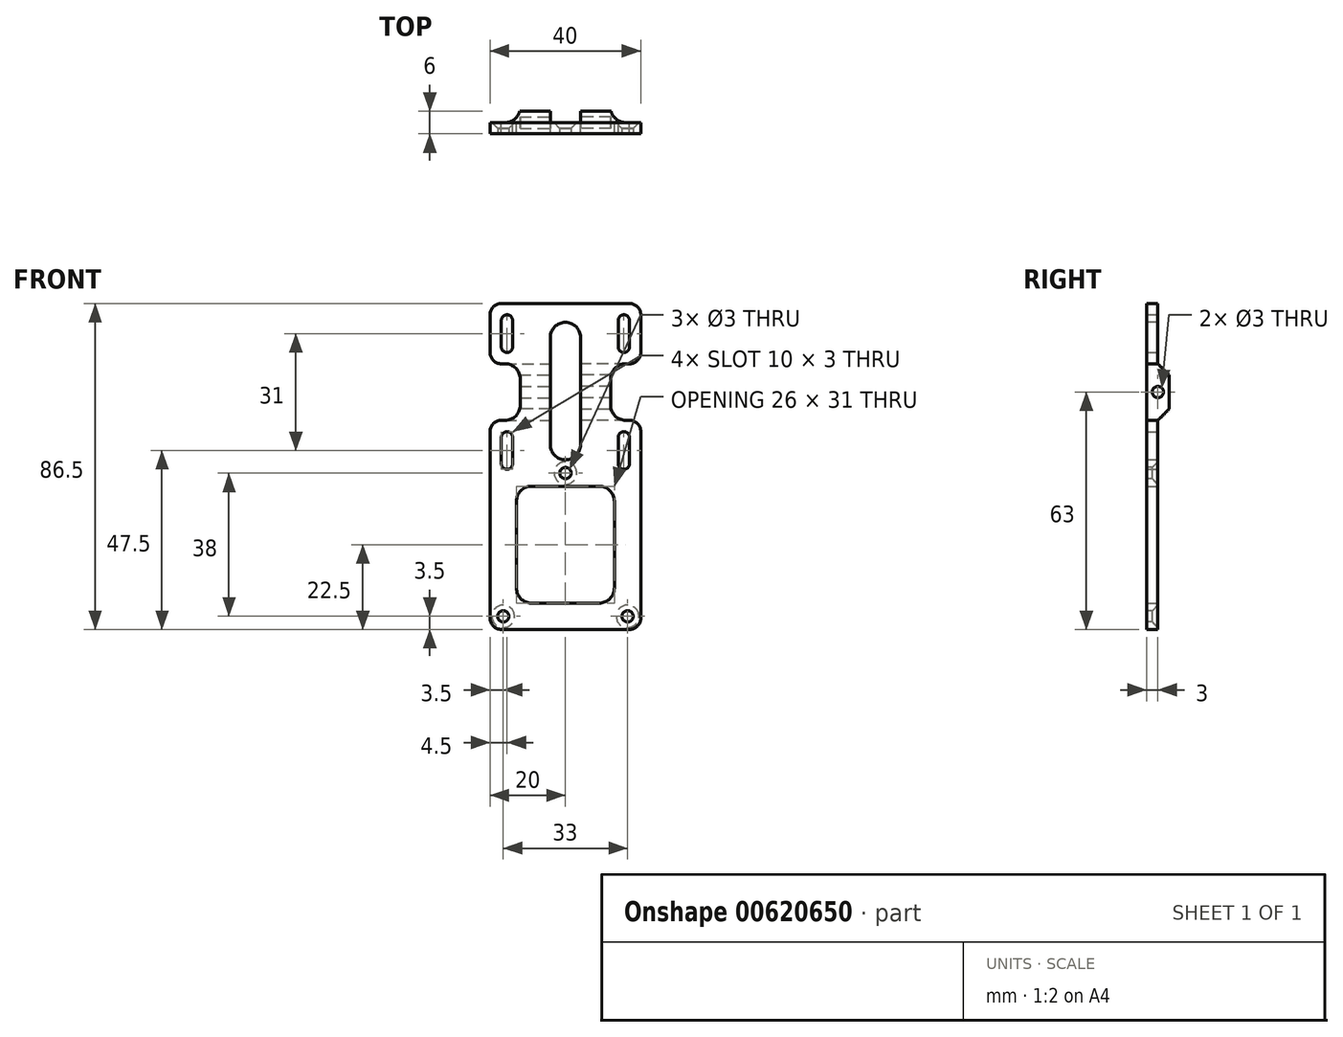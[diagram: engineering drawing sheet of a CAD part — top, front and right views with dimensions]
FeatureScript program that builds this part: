
annotation { "Feature Type Name" : "Feature", "Feature Type Description" : "" }
export const myFeature = defineFeature(function(context is Context, id is Id, definition is map)
    precondition{}
    {
        {
            var Q0;
            Q0=qCreatedBy(makeId("Front.planeOp"),FACE);
            var sketch = newSketch(context, id + "F0", { "sketchPlane" : qUnion([Q0])});
            skLineSegment(sketch, "E0.bottom", {"start": v(0, 43.25) * mm, "end": v(-20, 43.25) * mm});
            skLineSegment(sketch, "E0.top", {"start": v(0, -43.25) * mm, "end": v(-20, -43.25) * mm});
            skLineSegment(sketch, "E0.left", {"start": v(0, 43.25) * mm, "end": v(0, -43.25) * mm});
            skLineSegment(sketch, "E0.right", {"start": v(-20, 43.25) * mm, "end": v(-20, -43.25) * mm});
            skPoint(sketch, "E1", {"position": v(0, 0) * mm});
            skPoint(sketch, "E2", {"position": v(-16.5, -39.75) * mm});
            skPoint(sketch, "E3", {"position": v(0, -1.75) * mm});
            skLineSegment(sketch, "E4.bottom", {"start": v(-14, -0.75) * mm, "end": v(-17, -0.75) * mm});
            skLineSegment(sketch, "E4.top", {"start": v(-14, 9.25) * mm, "end": v(-17, 9.25) * mm});
            skLineSegment(sketch, "E4.left", {"start": v(-14, -0.75) * mm, "end": v(-14, 9.25) * mm});
            skLineSegment(sketch, "E4.right", {"start": v(-17, -0.75) * mm, "end": v(-17, 9.25) * mm});
            skLineSegment(sketch, "E5", {"start": v(0, 19.75) * mm, "end": v(-20, 19.75) * mm, "construction": true});
            skPoint(sketch, "E6", {"position": v(-14, 4.25) * mm});
            skLineSegment(sketch, "E7.MirrorCS", {"start": v(-14, 30.25) * mm, "end": v(-17, 30.25) * mm});
            skLineSegment(sketch, "E8.MirrorCS", {"start": v(-14, 40.25) * mm, "end": v(-14, 30.25) * mm});
            skLineSegment(sketch, "E9.MirrorCS", {"start": v(-17, 40.25) * mm, "end": v(-17, 30.25) * mm});
            skLineSegment(sketch, "E10.MirrorCS", {"start": v(-14, 40.25) * mm, "end": v(-17, 40.25) * mm});
            skLineSegment(sketch, "E11", {"start": v(0, 38.25) * mm, "end": v(-4, 38.25) * mm});
            skLineSegment(sketch, "E12", {"start": v(-4, 38.25) * mm, "end": v(-4, 1.75) * mm});
            skLineSegment(sketch, "E13", {"start": v(-4, 1.75) * mm, "end": v(0, 1.75) * mm});
            skLineSegment(sketch, "E14", {"start": v(0, -36.25) * mm, "end": v(-13, -36.25) * mm});
            skLineSegment(sketch, "E15", {"start": v(-13, -36.25) * mm, "end": v(-13, -5.25) * mm});
            skLineSegment(sketch, "E16", {"start": v(-13, -5.25) * mm, "end": v(0, -5.25) * mm});
            skPoint(sketch, "E17", {"position": v(-15.5, -0.75) * mm});
            skLineSegment(sketch, "E18", {"start": v(-20, 12.25) * mm, "end": v(-12, 12.25) * mm});
            skLineSegment(sketch, "E19", {"start": v(-12, 12.25) * mm, "end": v(-12, 19.75) * mm});
            skLineSegment(sketch, "E20.MirrorCS", {"start": v(-12, 27.25) * mm, "end": v(-12, 19.75) * mm});
            skLineSegment(sketch, "E21.MirrorCS", {"start": v(-20, 27.25) * mm, "end": v(-12, 27.25) * mm});
            skLineSegment(sketch, "E22", {"start": v(-12, 27.25) * mm, "end": v(-4, 27.25) * mm});
            skLineSegment(sketch, "E23", {"start": v(-12, 12.25) * mm, "end": v(-4, 12.25) * mm});
            skSolve(sketch);
        }
        {
            var Q0;
            Q0=makeQuery(id+"F0.imprint","IMPRINT",FACE,{"disambiguationData":[TD([[makeQuery(id+"F0.imprint","IMPRINT",EDGE,{"derivedFrom":sQuery(id+"F0.wireOp",EDGE,"E0.bottom")}),1.0]])]});
            var Q1;
            {var subQ0=sQuery(id+"F0.wireOp",EDGE,"vfTZMCeK-eEZJ-BKLE-hduP-PeNeDjFpHONc");Q1=makeQuery(id+"F0.imprint","IMPRINT",FACE,{"disambiguationData":[TD([[makeQuery(id+"F0.imprint","IMPRINT",EDGE,{"derivedFrom":subQ0}),-1.0]])]});}
            var Q2;
            {var subQ3=sQuery(id+"F0.wireOp",EDGE,"E0.top");Q2=makeQuery(id+"F0.imprint","IMPRINT",FACE,{"disambiguationData":[TD([[makeQuery(id+"F0.imprint","IMPRINT",EDGE,{"derivedFrom":subQ3}),-1.0]])]});}
            var Q3;
            Q3=makeQuery(id+"F0.imprint","IMPRINT",FACE,{"disambiguationData":[TD([[makeQuery(id+"F0.imprint","IMPRINT",EDGE,{"derivedFrom":sQuery(id+"F0.wireOp",EDGE,"E19")}),-1.0]])]});
            extrude(context, id + "F1", {"entities" : qUnion([Q0, Q1, Q2, Q3]), "depth" : 3 * mm, "offsetDistance" : 25 * mm});
        }
        {
            var Q0;
            Q0=sQuery(id+"F0.wireOp",VERTEX,"E3");
            var Q1;
            Q1=sQuery(id+"F0.wireOp",VERTEX,"E2");
            var Q2;
            Q2=makeQuery(id+"F1.opExtrude","SWEPT_BODY",BODY,{"disambiguationData":[OSD([sQuery(id+"F0.wireOp",EDGE,"E0.bottom"),sQuery(id+"F0.wireOp",EDGE,"E0.top"),sQuery(id+"F0.wireOp",EDGE,"E0.left"),sQuery(id+"F0.wireOp",EDGE,"E0.right"),sQuery(id+"F0.wireOp",EDGE,"E4.bottom"),sQuery(id+"F0.wireOp",EDGE,"E4.top"),sQuery(id+"F0.wireOp",EDGE,"E4.left"),sQuery(id+"F0.wireOp",EDGE,"E4.right"),sQuery(id+"F0.wireOp",EDGE,"E7.MirrorCS"),sQuery(id+"F0.wireOp",EDGE,"E8.MirrorCS"),sQuery(id+"F0.wireOp",EDGE,"E9.MirrorCS"),sQuery(id+"F0.wireOp",EDGE,"E10.MirrorCS")])]});
            hole(context, id + "F2", {"style" : HoleStyle.C_SINK, "endStyle" : HoleEndStyle.THROUGH, "oppositeDirection" : true, "holeDiameter" : 3 * mm, "cSinkDiameter" : 6 * mm, "cSinkAngle" : 90 * degree, "majorDiameter" : 5 * mm, "isTappedThrough" : true, "tappedDepth" : 12 * mm, "tapClearance" : 3, "locations" : qUnion([Q0, Q1]), "scope" : qUnion([Q2]), "startStyle" : HoleStartStyle.PART});
        }
        {
            var Q0;
            Q0=makeQuery(id+"F1.opExtrude","SWEPT_EDGE",EDGE,{"disambiguationData":[OSD([sQuery(id+"F0.wireOp",EDGE,"E4.bottom"),sQuery(id+"F0.wireOp",EDGE,"E4.left")])]});
            var Q1;
            Q1=makeQuery(id+"F1.opExtrude","SWEPT_EDGE",EDGE,{"disambiguationData":[OSD([sQuery(id+"F0.wireOp",EDGE,"E4.bottom"),sQuery(id+"F0.wireOp",EDGE,"E4.right")])]});
            var Q2;
            Q2=makeQuery(id+"F1.opExtrude","SWEPT_EDGE",EDGE,{"disambiguationData":[OSD([sQuery(id+"F0.wireOp",EDGE,"E4.top"),sQuery(id+"F0.wireOp",EDGE,"E4.right")])]});
            var Q3;
            Q3=makeQuery(id+"F1.opExtrude","SWEPT_EDGE",EDGE,{"disambiguationData":[OSD([sQuery(id+"F0.wireOp",EDGE,"E4.top"),sQuery(id+"F0.wireOp",EDGE,"E4.left")])]});
            var Q4;
            Q4=makeQuery(id+"F1.opExtrude","SWEPT_EDGE",EDGE,{"disambiguationData":[OSD([sQuery(id+"F0.wireOp",EDGE,"E8.MirrorCS"),sQuery(id+"F0.wireOp",EDGE,"E10.MirrorCS")])]});
            var Q5;
            Q5=makeQuery(id+"F1.opExtrude","SWEPT_EDGE",EDGE,{"disambiguationData":[OSD([sQuery(id+"F0.wireOp",EDGE,"E9.MirrorCS"),sQuery(id+"F0.wireOp",EDGE,"E10.MirrorCS")])]});
            var Q6;
            Q6=makeQuery(id+"F1.opExtrude","SWEPT_EDGE",EDGE,{"disambiguationData":[OSD([sQuery(id+"F0.wireOp",EDGE,"E7.MirrorCS"),sQuery(id+"F0.wireOp",EDGE,"E9.MirrorCS")])]});
            var Q7;
            Q7=makeQuery(id+"F1.opExtrude","SWEPT_EDGE",EDGE,{"disambiguationData":[OSD([sQuery(id+"F0.wireOp",EDGE,"E7.MirrorCS"),sQuery(id+"F0.wireOp",EDGE,"E8.MirrorCS")])]});
            fillet(context, id + "F3", {"entities" : qUnion([Q0, Q1, Q2, Q3, Q4, Q5, Q6, Q7]), "radius" : 1.5 * mm, "tangentPropagation" : true, "allowEdgeOverflow" : false});
        }
        {
            var Q0;
            Q0=makeQuery(id+"F1.opExtrude","SWEPT_EDGE",EDGE,{"disambiguationData":[OSD([sQuery(id+"F0.wireOp",EDGE,"E0.bottom"),sQuery(id+"F0.wireOp",EDGE,"E0.right")])]});
            var Q1;
            Q1=makeQuery(id+"F1.opExtrude","SWEPT_EDGE",EDGE,{"disambiguationData":[OSD([sQuery(id+"F0.wireOp",EDGE,"E0.top"),sQuery(id+"F0.wireOp",EDGE,"E0.right")])]});
            var Q2;
            Q2=makeQuery(id+"F1.opExtrude","SWEPT_EDGE",EDGE,{"disambiguationData":[OSD([sQuery(id+"F0.wireOp",EDGE,"E0.right"),sQuery(id+"F0.wireOp",EDGE,"E18")])]});
            var Q3;
            Q3=makeQuery(id+"F1.opExtrude","SWEPT_EDGE",EDGE,{"disambiguationData":[OSD([sQuery(id+"F0.wireOp",EDGE,"E0.right"),sQuery(id+"F0.wireOp",EDGE,"E21.MirrorCS")])]});
            fillet(context, id + "F4", {"entities" : qUnion([Q0, Q1, Q2, Q3]), "radius" : 3 * mm, "tangentPropagation" : true, "allowEdgeOverflow" : false});
        }
        {
            var Q0;
            Q0=makeQuery(id+"F0.imprint","IMPRINT",FACE,{"disambiguationData":[TD([[makeQuery(id+"F0.imprint","IMPRINT",EDGE,{"derivedFrom":sQuery(id+"F0.wireOp",EDGE,"E19")}),-1.0]])]});
            extrude(context, id + "F5", {"entities" : qUnion([Q0]), "operationType" : NewBodyOperationType.ADD, "oppositeDirection" : true, "depth" : 3 * mm, "offsetDistance" : 25 * mm});
        }
        {
            var Q0;
            Q0=makeQuery(id+"F5.opExtrude","CAP_EDGE",EDGE,{"disambiguationData":[OSD([sQuery(id+"F0.wireOp",EDGE,"E23")])],"isStart":false});
            var Q1;
            Q1=makeQuery(id+"F5.opExtrude","CAP_EDGE",EDGE,{"disambiguationData":[OSD([sQuery(id+"F0.wireOp",EDGE,"E22")])],"isStart":false});
            chamfer(context, id + "F6", {"entities" : qUnion([Q0, Q1]), "width" : 3 * mm, "tangentPropagation" : true});
        }
        {
            var Q0;
            Q0=makeQuery(id+"F1.opExtrude","SWEPT_EDGE",EDGE,{"disambiguationData":[OSD([sQuery(id+"F0.wireOp",EDGE,"E12"),sQuery(id+"F0.wireOp",EDGE,"E13")])]});
            var Q1;
            Q1=makeQuery(id+"F1.opExtrude","SWEPT_EDGE",EDGE,{"disambiguationData":[OSD([sQuery(id+"F0.wireOp",EDGE,"E11"),sQuery(id+"F0.wireOp",EDGE,"E12")])]});
            var Q2;
            Q2=makeQuery(id+"F1.opExtrude","SWEPT_EDGE",EDGE,{"disambiguationData":[OSD([sQuery(id+"F0.wireOp",EDGE,"E15"),sQuery(id+"F0.wireOp",EDGE,"E16")])]});
            var Q3;
            Q3=makeQuery(id+"F1.opExtrude","SWEPT_EDGE",EDGE,{"disambiguationData":[OSD([sQuery(id+"F0.wireOp",EDGE,"E14"),sQuery(id+"F0.wireOp",EDGE,"E15")])]});
            var Q4;
            Q4=makeQuery(id+"F1.opExtrude","SWEPT_EDGE",EDGE,{"disambiguationData":[OSD([sQuery(id+"F0.wireOp",EDGE,"E20.MirrorCS"),sQuery(id+"F0.wireOp",EDGE,"E21.MirrorCS"),sQuery(id+"F0.wireOp",EDGE,"E22")])]});
            var Q5;
            Q5=makeQuery(id+"F1.opExtrude","SWEPT_EDGE",EDGE,{"disambiguationData":[OSD([sQuery(id+"F0.wireOp",EDGE,"E18"),sQuery(id+"F0.wireOp",EDGE,"E19"),sQuery(id+"F0.wireOp",EDGE,"E23")])]});
            fillet(context, id + "F7", {"entities" : qUnion([Q0, Q1, Q2, Q3, Q4, Q5]), "radius" : 4 * mm, "tangentPropagation" : true, "allowEdgeOverflow" : false});
        }
        {
            var Q0;
            {var subQ0=sQuery(id+"F0.wireOp",EDGE,"E20.MirrorCS");var subQ1=sQuery(id+"F0.wireOp",EDGE,"E19");Q0=makeQuery(id+"F5.boolean.opBoolean","MERGE",FACE,{"derivedFrom":[makeQuery(id+"F1.opExtrude","SWEPT_FACE",FACE,{"disambiguationData":[OSD([subQ1,subQ0])]}),makeQuery(id+"F5.opExtrude","SWEPT_FACE",FACE,{"disambiguationData":[OSD([subQ1,subQ0])]})]});}
            var sketch = newSketch(context, id + "F8", { "sketchPlane" : qUnion([Q0])});
            skPoint(sketch, "E24", {"position": v(0, 19.75) * mm});
            skPoint(sketch, "E24.positionSnap0", {"position": v(0, 23.25) * mm});
            skPoint(sketch, "E24.positionSnap1", {"position": v(3, 19.75) * mm});
            skSolve(sketch);
        }
        {
            var Q0;
            Q0=sQuery(id+"F8.wireOp",VERTEX,"E24");
            var Q1;
            Q1=makeQuery(id+"F1.opExtrude","SWEPT_BODY",BODY,{"disambiguationData":[OSD([sQuery(id+"F0.wireOp",EDGE,"E0.bottom"),sQuery(id+"F0.wireOp",EDGE,"E0.top"),sQuery(id+"F0.wireOp",EDGE,"E0.left"),sQuery(id+"F0.wireOp",EDGE,"E0.right"),sQuery(id+"F0.wireOp",EDGE,"E4.bottom"),sQuery(id+"F0.wireOp",EDGE,"E4.top"),sQuery(id+"F0.wireOp",EDGE,"E4.left"),sQuery(id+"F0.wireOp",EDGE,"E4.right"),sQuery(id+"F0.wireOp",EDGE,"E7.MirrorCS"),sQuery(id+"F0.wireOp",EDGE,"E8.MirrorCS"),sQuery(id+"F0.wireOp",EDGE,"E9.MirrorCS"),sQuery(id+"F0.wireOp",EDGE,"E10.MirrorCS"),sQuery(id+"F0.wireOp",EDGE,"E11"),sQuery(id+"F0.wireOp",EDGE,"E12"),sQuery(id+"F0.wireOp",EDGE,"E13"),sQuery(id+"F0.wireOp",EDGE,"E14"),sQuery(id+"F0.wireOp",EDGE,"E15"),sQuery(id+"F0.wireOp",EDGE,"E16"),sQuery(id+"F0.wireOp",EDGE,"E18"),sQuery(id+"F0.wireOp",EDGE,"E19"),sQuery(id+"F0.wireOp",EDGE,"E20.MirrorCS"),sQuery(id+"F0.wireOp",EDGE,"E21.MirrorCS")])]});
            hole(context, id + "F9", {"style" : HoleStyle.SIMPLE, "endStyle" : HoleEndStyle.THROUGH, "holeDiameter" : 3 * mm, "majorDiameter" : 5 * mm, "isTappedThrough" : true, "tappedDepth" : 12 * mm, "tapClearance" : 3, "locations" : qUnion([Q0]), "scope" : qUnion([Q1]), "startStyle" : HoleStartStyle.PART});
        }
        {
            var Q0;
            Q0=makeQuery(id+"F1.opExtrude","SWEPT_BODY",BODY,{"disambiguationData":[OSD([sQuery(id+"F0.wireOp",EDGE,"E0.bottom"),sQuery(id+"F0.wireOp",EDGE,"E0.top"),sQuery(id+"F0.wireOp",EDGE,"E0.left"),sQuery(id+"F0.wireOp",EDGE,"E0.right"),sQuery(id+"F0.wireOp",EDGE,"E4.bottom"),sQuery(id+"F0.wireOp",EDGE,"E4.top"),sQuery(id+"F0.wireOp",EDGE,"E4.left"),sQuery(id+"F0.wireOp",EDGE,"E4.right"),sQuery(id+"F0.wireOp",EDGE,"E7.MirrorCS"),sQuery(id+"F0.wireOp",EDGE,"E8.MirrorCS"),sQuery(id+"F0.wireOp",EDGE,"E9.MirrorCS"),sQuery(id+"F0.wireOp",EDGE,"E10.MirrorCS"),sQuery(id+"F0.wireOp",EDGE,"E11"),sQuery(id+"F0.wireOp",EDGE,"E12"),sQuery(id+"F0.wireOp",EDGE,"E13")])]});
            var Q1;
            Q1=qCreatedBy(makeId("Right.planeOp"),FACE);
            mirror(context, id + "F10", {"operationType" : NewBodyOperationType.ADD, "entities" : qUnion([Q0]), "mirrorPlane" : qUnion([Q1])});
        }
    });
